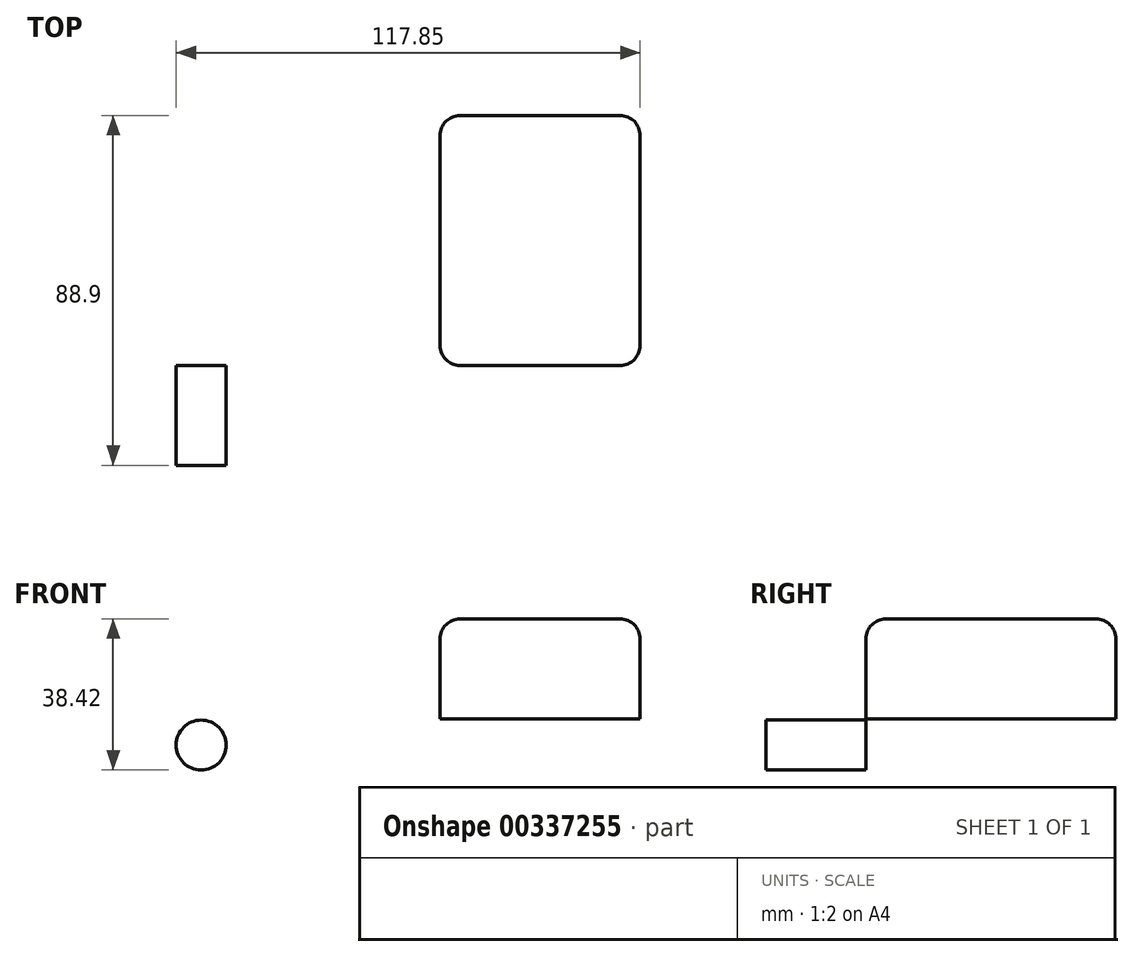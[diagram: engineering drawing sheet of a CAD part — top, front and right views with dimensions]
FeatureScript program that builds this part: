
annotation { "Feature Type Name" : "Feature", "Feature Type Description" : "" }
export const myFeature = defineFeature(function(context is Context, id is Id, definition is map)
    precondition{}
    {
        {
            var Q0;
            Q0=qCreatedBy(makeId("Top.planeOp"),FACE);
            var sketch = newSketch(context, id + "F0", { "sketchPlane" : qUnion([Q0])});
            skLineSegment(sketch, "E0.bottom", {"start": v(0, 0) * mm, "end": v(50.8, 0) * mm});
            skLineSegment(sketch, "E0.top", {"start": v(0, 63.5) * mm, "end": v(50.8, 63.5) * mm});
            skLineSegment(sketch, "E0.left", {"start": v(0, 0) * mm, "end": v(0, 63.5) * mm});
            skLineSegment(sketch, "E0.right", {"start": v(50.8, 0) * mm, "end": v(50.8, 63.5) * mm});
            skSolve(sketch);
        }
        {
            var Q0;
            Q0 = qSketchRegion(id + "F0", true);
            extrude(context, id + "F1", {"entities" : qUnion([Q0]), "depth" : 25.4 * mm});
        }
        {
            var Q0;
            Q0=qCreatedBy(makeId("Front.planeOp"),FACE);
            var sketch = newSketch(context, id + "F2", { "sketchPlane" : qUnion([Q0])});
            skCircle(sketch, "E1", {"center": v(-60.7, -6.67) * mm, "radius": 6.35 * mm});
            skSolve(sketch);
        }
        {
            var Q0;
            Q0 = qSketchRegion(id + "F2", true);
            extrude(context, id + "F3", {"entities" : qUnion([Q0]), "depth" : 25.4 * mm});
        }
        {
            var Q0;
            Q0=makeQuery(id+"F1.opExtrude","CAP_EDGE",EDGE,{"disambiguationData":[OSD([sQuery(id+"F0.wireOp",EDGE,"E0.bottom")])],"isStart":false});
            var Q1;
            Q1=makeQuery(id+"F1.opExtrude","CAP_EDGE",EDGE,{"disambiguationData":[OSD([sQuery(id+"F0.wireOp",EDGE,"E0.right")])],"isStart":false});
            var Q2;
            Q2=makeQuery(id+"F1.opExtrude","CAP_EDGE",EDGE,{"disambiguationData":[OSD([sQuery(id+"F0.wireOp",EDGE,"E0.top")])],"isStart":false});
            var Q3;
            Q3=makeQuery(id+"F1.opExtrude","CAP_EDGE",EDGE,{"disambiguationData":[OSD([sQuery(id+"F0.wireOp",EDGE,"E0.left")])],"isStart":false});
            fillet(context, id + "F4", {"entities" : qUnion([Q0, Q1, Q2, Q3]), "radius" : 5.08 * mm, "tangentPropagation" : true, "allowEdgeOverflow" : false});
        }
        {
            var Q0;
            Q0=makeQuery(id+"F1.opExtrude","SWEPT_EDGE",EDGE,{"disambiguationData":[OSD([sQuery(id+"F0.wireOp",EDGE,"E0.bottom"),sQuery(id+"F0.wireOp",EDGE,"E0.left")])]});
            var Q1;
            Q1=makeQuery(id+"F1.opExtrude","SWEPT_EDGE",EDGE,{"disambiguationData":[OSD([sQuery(id+"F0.wireOp",EDGE,"E0.bottom"),sQuery(id+"F0.wireOp",EDGE,"E0.right")])]});
            var Q2;
            Q2=makeQuery(id+"F1.opExtrude","SWEPT_EDGE",EDGE,{"disambiguationData":[OSD([sQuery(id+"F0.wireOp",EDGE,"E0.top"),sQuery(id+"F0.wireOp",EDGE,"E0.right")])]});
            var Q3;
            Q3=makeQuery(id+"F1.opExtrude","SWEPT_EDGE",EDGE,{"disambiguationData":[OSD([sQuery(id+"F0.wireOp",EDGE,"E0.top"),sQuery(id+"F0.wireOp",EDGE,"E0.left")])]});
            fillet(context, id + "F5", {"entities" : qUnion([Q0, Q1, Q2, Q3]), "radius" : 5.08 * mm, "tangentPropagation" : true, "allowEdgeOverflow" : false});
        }
    });
